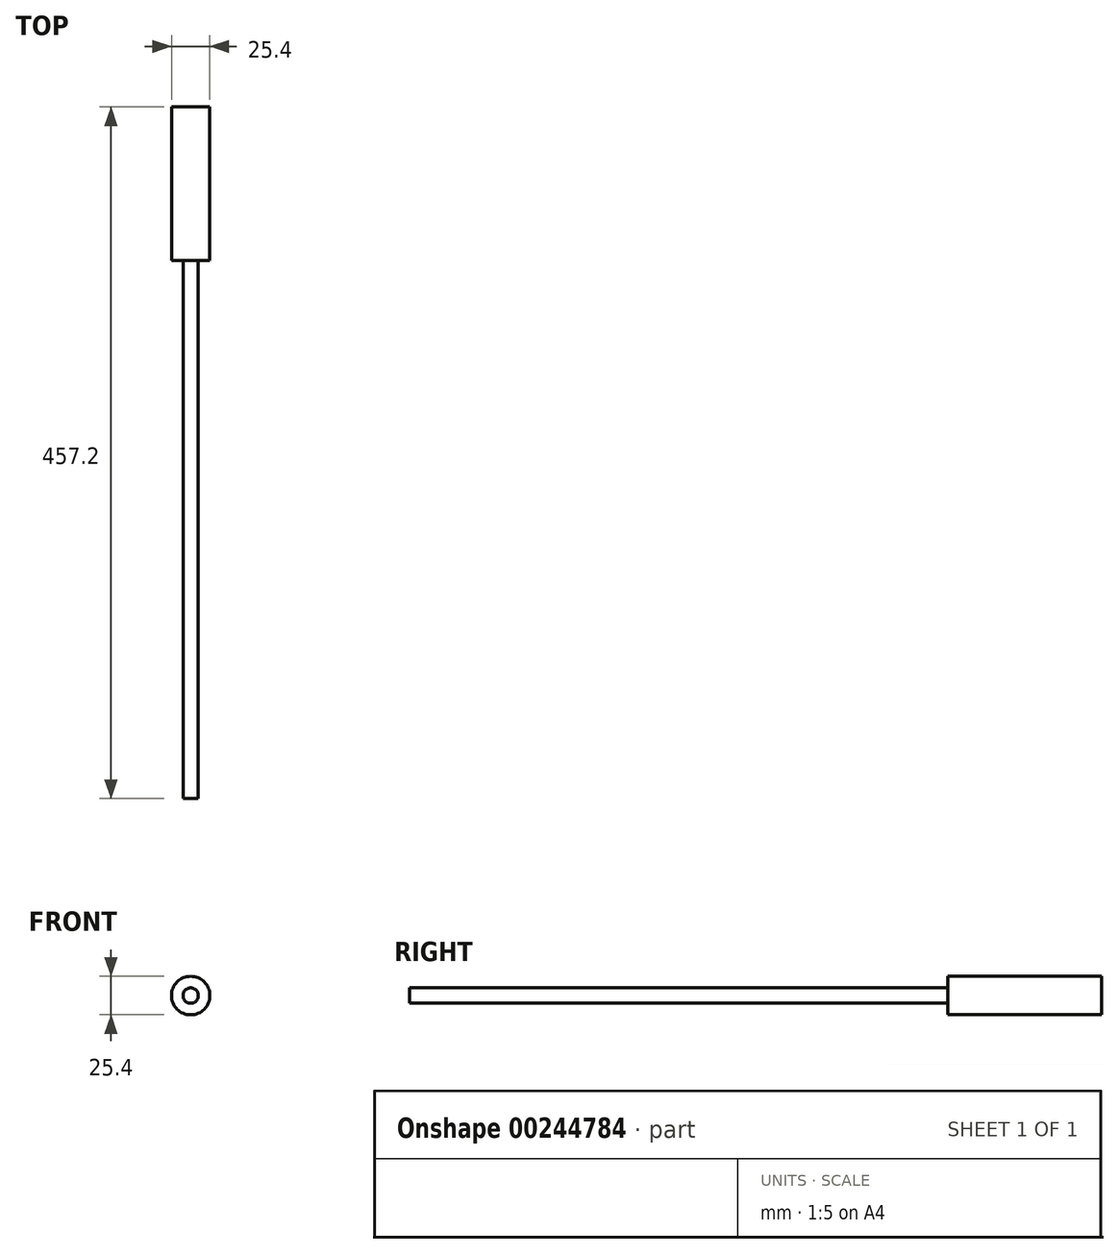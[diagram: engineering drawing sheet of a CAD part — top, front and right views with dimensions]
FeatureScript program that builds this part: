
annotation { "Feature Type Name" : "Feature", "Feature Type Description" : "" }
export const myFeature = defineFeature(function(context is Context, id is Id, definition is map)
    precondition{}
    {
        {
            var Q0;
            Q0=qCreatedBy(makeId("Front.planeOp"),FACE);
            var sketch = newSketch(context, id + "F0", { "sketchPlane" : qUnion([Q0])});
            skCircle(sketch, "E0", {"center": v(0, 0) * mm, "radius": 12.7 * mm});
            skSolve(sketch);
        }
        {
            var Q0;
            Q0=makeQuery(id+"F0.imprint","IMPRINT",FACE,{"disambiguationData":[TD([[makeQuery(id+"F0.imprint","IMPRINT",EDGE,{"derivedFrom":sQuery(id+"F0.wireOp",EDGE,"E0")}),1.0]])]});
            extrude(context, id + "F1", {"entities" : qUnion([Q0]), "oppositeDirection" : true, "depth" : 101.6 * mm});
        }
        {
            var Q0;
            Q0=makeQuery(id+"F1.opExtrude","CAP_FACE",FACE,{"disambiguationData":[OSD([sQuery(id+"F0.wireOp",EDGE,"E0")])],"isStart":true});
            var sketch = newSketch(context, id + "F2", { "sketchPlane" : qUnion([Q0])});
            skCircle(sketch, "E1", {"center": v(0, 0) * mm, "radius": 5.08 * mm});
            skSolve(sketch);
        }
        {
            var Q0;
            Q0=makeQuery(id+"F2.imprint","IMPRINT",FACE,{"disambiguationData":[TD([[makeQuery(id+"F2.imprint","IMPRINT",EDGE,{"derivedFrom":sQuery(id+"F2.wireOp",EDGE,"E1")}),1.0]])]});
            extrude(context, id + "F3", {"entities" : qUnion([Q0]), "operationType" : NewBodyOperationType.ADD, "depth" : 355.6 * mm});
        }
    });
